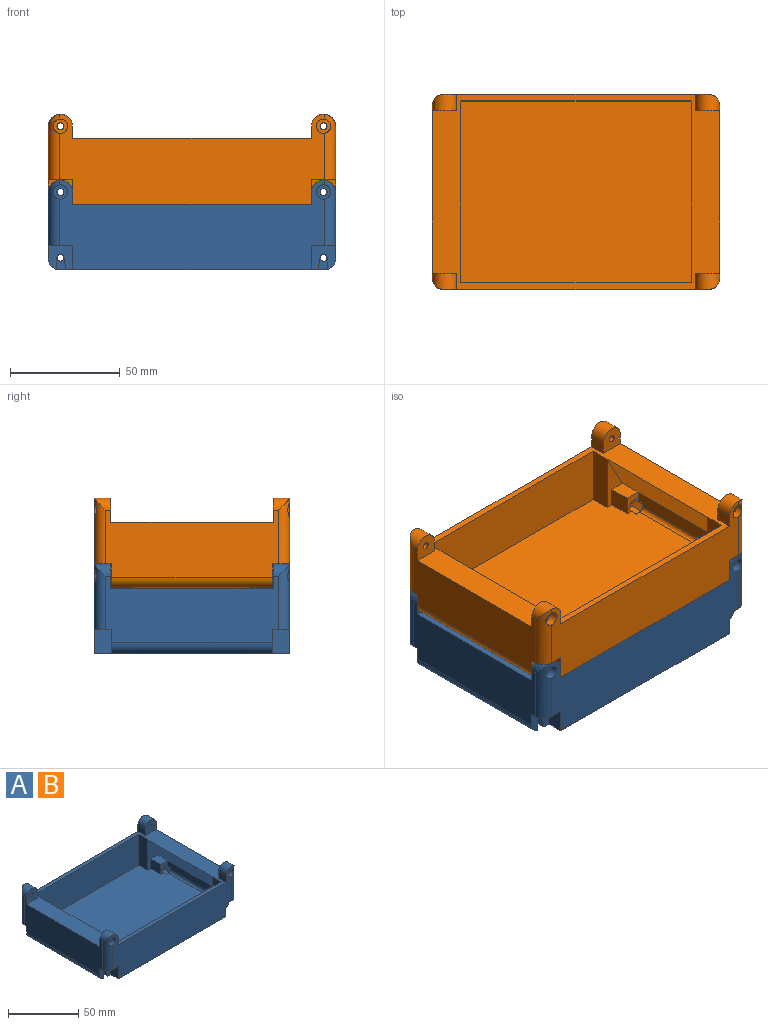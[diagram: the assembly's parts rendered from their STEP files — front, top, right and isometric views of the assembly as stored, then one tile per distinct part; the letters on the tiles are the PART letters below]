
ASSEMBLY  parts=2 mates=1
PART A: 125 faces, bbox 131x89x41 mm
  f0: cylinder r=1.6mm len=11.3mm, axis (0,-1,0), area 60.7mm2, adj f2,f120,f122,f123,f124
  f1: cylinder r=5mm len=73.6mm, axis (0,1,0), area 555.9mm2, adj f2,f8,f32,f33,f108,f110,f122,f124
  f2: plane 11.2x11mm, normal (0,-1,0), area 93.6mm2, adj f0,f1,f32,f33,f45,f46,f122,f123
  f3: plane 121x83mm, normal (0,0,1), area 9527.3mm2, adj f5,f19,f28,f29,f30,f31,f34,f35
  f4: plane 45x6.54mm, normal (-1,0,0), area 283.4mm2, adj f5,f34,f60,f64,f100,f107,f114,f121
  f5: plane 8.54x7mm, normal (0,1,0), area 34mm2, adj f3,f4,f58,f59,f114,f117,f118,f119
  f6: plane 121x41mm, normal (0,-1,0), area 3573mm2, adj f7,f14,f25,f26,f33,f40,f45,f46
  f7: cylinder r=5mm len=29.98mm, axis (0,0,-1), area 205.2mm2, adj f6,f32,f46,f65,f113
  f8: plane 11.2x11mm, normal (0,1,0), area 93.6mm2, adj f1,f9,f32,f33,f47,f48,f108,f109
  f9: cylinder r=1.6mm len=11.3mm, axis (0,1,0), area 60.7mm2, adj f8,f106,f108,f109,f110
  f10: plane 121x41mm, normal (0,1,0), area 3573mm2, adj f11,f20,f33,f36,f39,f40,f47,f48
  f11: cylinder r=5mm len=29.98mm, axis (0,0,-1), area 205.2mm2, adj f10,f32,f48,f68,f99
  f12: plane 11.2x11mm, normal (0,-1,0), area 93.6mm2, adj f13,f16,f27,f33,f49,f50,f94,f95
  f13: cylinder r=1.6mm len=11.3mm, axis (0,-1,0), area 60.7mm2, adj f12,f93,f94,f95,f96
  f14: cylinder r=5mm len=29.98mm, axis (0,0,-1), area 205.2mm2, adj f6,f27,f50,f67,f85
  f15: cylinder r=1.6mm len=11.3mm, axis (0,1,0), area 60.7mm2, adj f17,f79,f80,f81,f82
  f16: cylinder r=5mm len=73.6mm, axis (0,-1,0), area 555.9mm2, adj f12,f17,f27,f33,f80,f82,f94,f96
  f17: plane 11.2x11mm, normal (0,1,0), area 93.6mm2, adj f15,f16,f27,f33,f51,f52,f80,f81
  f18: plane 45x6.54mm, normal (1,0,0), area 283.4mm2, adj f19,f38,f53,f63,f72,f73,f86,f87
  f19: plane 8.54x7mm, normal (0,-1,0), area 34mm2, adj f3,f18,f56,f57,f73,f76,f77,f78
  f20: cylinder r=5mm len=29.98mm, axis (0,0,-1), area 205.2mm2, adj f10,f27,f52,f66,f71
  f21: plane 11x11mm, normal (0,1,0), area 100mm2, adj f25,f32,f40,f65,f111
  f22: plane 11x11mm, normal (0,-1,0), area 100mm2, adj f32,f36,f40,f68,f97
  f23: plane 11x11mm, normal (0,1,0), area 100mm2, adj f26,f27,f40,f67,f83
  f24: plane 11x11mm, normal (0,-1,0), area 100mm2, adj f27,f39,f40,f66,f69
  f25: plane 7.5x5.5mm, normal (-1,0,0), area 41.2mm2, adj f6,f21,f40,f65
  f26: plane 7.5x5.5mm, normal (1,0,0), area 41.2mm2, adj f6,f23,f40,f67
  f27: plane 79x30.5mm, normal (-1,0,0), area 1970.1mm2, adj f12,f14,f16,f17,f20,f23,f24,f40
  f28: plane 27x10mm, normal (0,1,0), area 117.9mm2, adj f3,f44,f58,f59,f64
  f29: plane 27x10mm, normal (0,1,0), area 117.9mm2, adj f3,f42,f54,f55,f63
  f30: plane 27x10mm, normal (0,-1,0), area 117.9mm2, adj f3,f43,f61,f62,f64
  f31: plane 27x10mm, normal (0,-1,0), area 117.9mm2, adj f3,f41,f56,f57,f63
  f32: plane 79x30.5mm, normal (1,0,0), area 1970.1mm2, adj f1,f2,f7,f8,f11,f21,f22,f40
  f33: plane 121x89mm, normal (0,0,-1), area 10456.2mm2, adj f1,f2,f6,f8,f10,f12,f16,f17
  f34: cylinder r=2mm len=39mm, axis (0,1,0), area 122.5mm2, adj f3,f4,f107,f121
  f35: plane 105x27mm, normal (0,1,0), area 2835mm2, adj f3,f40,f42,f44
  f36: plane 7.5x5.5mm, normal (-1,0,0), area 41.2mm2, adj f10,f22,f40,f68
  f37: plane 105x27mm, normal (0,-1,0), area 2835mm2, adj f3,f40,f41,f43
  f38: cylinder r=2mm len=39mm, axis (0,-1,0), area 122.5mm2, adj f3,f18,f72,f86
  f39: plane 7.5x5.5mm, normal (1,0,0), area 41.2mm2, adj f10,f24,f40,f66
  f40: plane 131x89mm, normal (0,0,1), area 2614mm2, adj f6,f10,f21,f22,f23,f24,f25,f26
  f41: plane 27x9mm, normal (1,0,0), area 243mm2, adj f3,f31,f37,f40
  f42: plane 27x9mm, normal (1,0,0), area 243mm2, adj f3,f29,f35,f40
  f43: plane 27x9mm, normal (-1,0,0), area 243mm2, adj f3,f30,f37,f40
  f44: plane 27x9mm, normal (-1,0,0), area 243mm2, adj f3,f28,f35,f40
  f45: plane 11x7.7mm, normal (1,0,0), area 84.7mm2, adj f2,f6,f33,f46
  f46: plane 11.2x7.7mm, normal (0,0,-1), area 80.9mm2, adj f2,f6,f7,f32,f45
  f47: plane 11x7.7mm, normal (1,0,0), area 84.7mm2, adj f8,f10,f33,f48
  f48: plane 11.2x7.7mm, normal (0,0,-1), area 80.9mm2, adj f8,f10,f11,f32,f47
  f49: plane 11x7.7mm, normal (-1,0,0), area 84.7mm2, adj f6,f12,f33,f50
  f50: plane 11.2x7.7mm, normal (0,0,-1), area 80.9mm2, adj f6,f12,f14,f27,f49
  f51: plane 11x7.7mm, normal (-1,0,0), area 84.7mm2, adj f10,f17,f33,f52
  f52: plane 11.2x7.7mm, normal (0,0,-1), area 80.9mm2, adj f10,f17,f20,f27,f51
  f53: plane 8.54x7mm, normal (0,1,0), area 34mm2, adj f3,f18,f54,f55,f87,f88,f89,f90
  f54: plane 10x7mm, normal (0,0,1), area 70mm2, adj f29,f53,f55,f63
  f55: plane 10x8.54mm, normal (1,0,0), area 85.4mm2, adj f3,f29,f53,f54
  f56: plane 10x8.54mm, normal (1,0,0), area 85.4mm2, adj f3,f19,f31,f57
  f57: plane 10x7mm, normal (0,0,1), area 70mm2, adj f19,f31,f56,f63
  f58: plane 10x8.54mm, normal (-1,0,0), area 85.4mm2, adj f3,f5,f28,f59
  f59: plane 10x7mm, normal (0,0,1), area 70mm2, adj f5,f28,f58,f64
  f60: plane 8.54x7mm, normal (0,-1,0), area 34mm2, adj f3,f4,f61,f62,f100,f101,f102,f103
  f61: plane 10x7mm, normal (0,0,1), area 70mm2, adj f30,f60,f62,f64
  f62: plane 10x8.54mm, normal (-1,0,0), area 85.4mm2, adj f3,f30,f60,f61
  f63: plane 65x18.46mm, normal (0.88,0,-0.48), area 1364.8mm2, adj f18,f29,f31,f40,f54,f57
  f64: plane 65x18.46mm, normal (-0.88,0,-0.48), area 1364.8mm2, adj f4,f28,f30,f40,f59,f61
  f65: cylinder r=5.5mm len=11mm, axis (0,1,0), area 114.7mm2, adj f6,f7,f21,f25,f32
  f66: cylinder r=5.5mm len=11mm, axis (0,1,0), area 114.7mm2, adj f10,f20,f24,f27,f39
  f67: cylinder r=5.5mm len=11mm, axis (0,1,0), area 114.7mm2, adj f6,f14,f23,f26,f27
  f68: cylinder r=5.5mm len=11mm, axis (0,1,0), area 114.7mm2, adj f10,f11,f22,f32,f36
  f69: cylinder r=1.6mm len=3.68mm, axis (0,1,0), area 37mm2, adj f24,f70
  f70: plane 6.5x6.5mm, normal (0,1,0), area 25.1mm2, adj f69,f71
  f71: cylinder r=3.25mm len=6.5mm, axis (0,1,0), area 74.3mm2, adj f10,f20,f70
  f72: plane 5.06x4.11mm, normal (0,1,0), area 2.5mm2, adj f3,f18,f38,f73,f74,f75,f76
  f73: plane 6x2.81mm, normal (0.87,0,-0.5), area 14.3mm2, adj f18,f19,f72,f74,f78,f79
  f74: plane 6x2.81mm, normal (0.87,0,0.5), area 19.5mm2, adj f72,f73,f75,f79
  f75: plane 6x3.25mm, normal (0,0,1), area 19.5mm2, adj f72,f74,f76,f79
  f76: plane 6x2.81mm, normal (-0.87,0,0.5), area 10.8mm2, adj f3,f19,f72,f75,f77,f79
  f77: plane 3x2.81mm, normal (-0.87,0,-0.5), area 9.8mm2, adj f19,f76,f78,f79
  f78: plane 3.25x3mm, normal (0,0,-1), area 9.7mm2, adj f19,f73,f77,f79
  f79: plane 6.5x5.63mm, normal (0,-1,0), area 19.4mm2, adj f15,f73,f74,f75,f76,f77,f78
  f80: plane 10x5.38mm, normal (1,0,0), area 53.8mm2, adj f15,f16,f17,f82
  f81: plane 10x5.77mm, normal (-0.99,0,-0.17), area 58.5mm2, adj f15,f17,f33,f82
  f82: plane 5.76x4.15mm, normal (0,1,0), area 16.2mm2, adj f15,f16,f33,f80,f81
  f83: cylinder r=1.6mm len=3.68mm, axis (0,-1,0), area 37mm2, adj f23,f84
  f84: plane 6.5x6.5mm, normal (0,-1,0), area 25.1mm2, adj f83,f85
  f85: cylinder r=3.25mm len=6.5mm, axis (0,-1,0), area 74.3mm2, adj f6,f14,f84
  f86: plane 5.06x4.11mm, normal (0,-1,0), area 2.5mm2, adj f3,f18,f38,f87,f90,f91,f92
  f87: plane 6x2.81mm, normal (0.87,0,-0.5), area 14.3mm2, adj f18,f53,f86,f88,f92,f93
  f88: plane 3.25x3mm, normal (0,0,-1), area 9.7mm2, adj f53,f87,f89,f93
  f89: plane 3x2.81mm, normal (-0.87,0,-0.5), area 9.8mm2, adj f53,f88,f90,f93
  f90: plane 6x2.81mm, normal (-0.87,0,0.5), area 10.8mm2, adj f3,f53,f86,f89,f91,f93
  f91: plane 6x3.25mm, normal (0,0,1), area 19.5mm2, adj f86,f90,f92,f93
  f92: plane 6x2.81mm, normal (0.87,0,0.5), area 19.5mm2, adj f86,f87,f91,f93
  f93: plane 6.5x5.63mm, normal (0,1,0), area 19.4mm2, adj f13,f87,f88,f89,f90,f91,f92
  f94: plane 10x5.38mm, normal (1,0,0), area 53.8mm2, adj f12,f13,f16,f96
  f95: plane 10x5.77mm, normal (-0.99,0,-0.17), area 58.5mm2, adj f12,f13,f33,f96
  f96: plane 5.76x4.15mm, normal (0,-1,0), area 16.2mm2, adj f13,f16,f33,f94,f95
  f97: cylinder r=1.6mm len=3.68mm, axis (0,1,0), area 37mm2, adj f22,f98
  f98: plane 6.5x6.5mm, normal (0,1,0), area 25.1mm2, adj f97,f99
  f99: cylinder r=3.25mm len=6.5mm, axis (0,1,0), area 74.3mm2, adj f10,f11,f98
  f100: plane 6x2.81mm, normal (-0.87,0,-0.5), area 14.3mm2, adj f4,f60,f101,f105,f106,f107
  f101: plane 3.25x3mm, normal (0,0,-1), area 9.7mm2, adj f60,f100,f102,f106
  f102: plane 3x2.81mm, normal (0.87,0,-0.5), area 9.8mm2, adj f60,f101,f103,f106
  f103: plane 6x2.81mm, normal (0.87,0,0.5), area 10.8mm2, adj f3,f60,f102,f104,f106,f107
  f104: plane 6x3.25mm, normal (0,0,1), area 19.5mm2, adj f103,f105,f106,f107
  f105: plane 6x2.81mm, normal (-0.87,0,0.5), area 19.5mm2, adj f100,f104,f106,f107
  f106: plane 6.5x5.63mm, normal (0,-1,0), area 19.4mm2, adj f9,f100,f101,f102,f103,f104,f105
  f107: plane 5.06x4.11mm, normal (0,1,0), area 2.5mm2, adj f3,f4,f34,f100,f103,f104,f105
  f108: plane 10x5.38mm, normal (-1,0,0), area 53.8mm2, adj f1,f8,f9,f110
  f109: plane 10x5.77mm, normal (0.99,0,-0.17), area 58.5mm2, adj f8,f9,f33,f110
  f110: plane 5.76x4.15mm, normal (0,1,0), area 16.2mm2, adj f1,f9,f33,f108,f109
  f111: cylinder r=1.6mm len=3.68mm, axis (0,-1,0), area 37mm2, adj f21,f112
  f112: plane 6.5x6.5mm, normal (0,-1,0), area 25.1mm2, adj f111,f113
  f113: cylinder r=3.25mm len=6.5mm, axis (0,-1,0), area 74.3mm2, adj f6,f7,f112
  f114: plane 6x2.81mm, normal (-0.87,0,-0.5), area 14.3mm2, adj f4,f5,f115,f119,f120,f121
  f115: plane 6x2.81mm, normal (-0.87,0,0.5), area 19.5mm2, adj f114,f116,f120,f121
  f116: plane 6x3.25mm, normal (0,0,1), area 19.5mm2, adj f115,f117,f120,f121
  f117: plane 6x2.81mm, normal (0.87,0,0.5), area 10.8mm2, adj f3,f5,f116,f118,f120,f121
  f118: plane 3x2.81mm, normal (0.87,0,-0.5), area 9.8mm2, adj f5,f117,f119,f120
  f119: plane 3.25x3mm, normal (0,0,-1), area 9.7mm2, adj f5,f114,f118,f120
  f120: plane 6.5x5.63mm, normal (0,1,0), area 19.4mm2, adj f0,f114,f115,f116,f117,f118,f119
  f121: plane 5.06x4.11mm, normal (0,-1,0), area 2.5mm2, adj f3,f4,f34,f114,f115,f116,f117
  f122: plane 10x5.38mm, normal (-1,0,0), area 53.8mm2, adj f0,f1,f2,f124
  f123: plane 10x5.77mm, normal (0.99,0,-0.17), area 58.5mm2, adj f0,f2,f33,f124
  f124: plane 5.76x4.15mm, normal (0,-1,0), area 16.2mm2, adj f0,f1,f33,f122,f123
PART B: same geometry as A
PLACE A t=(-7.7,9.82,-22.14)mm
PLACE B t=(-7.7,9.77,7.86)mm
MATE fastened B.f15 <-> A.f66  axis (0,1,0) through (-57.7,40.07,13.36)mm
